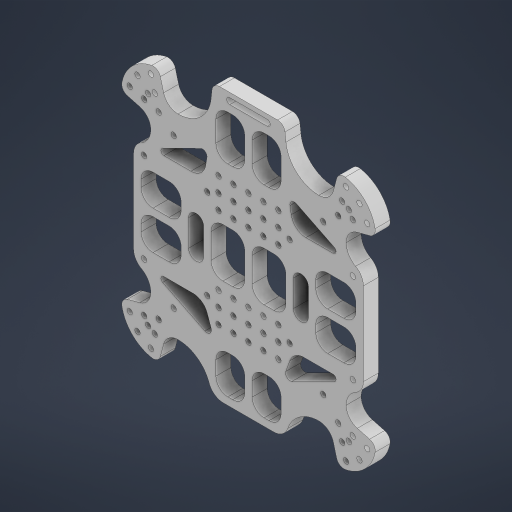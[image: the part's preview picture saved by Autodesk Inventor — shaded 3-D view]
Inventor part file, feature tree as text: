
AUTODESK INVENTOR PART (.ipt)
format: ipt  version: 2023 (Build 270158000, 158)  size: 738,816 bytes
history: native  units: mm
features: reference x147, extrude x5, fillet x4, sketch x4, other x4, plane x1
ambient origin geometry x8: Origin, YZ Plane, XZ Plane, XY Plane, X Axis, Y Axis, Z Axis, Center Point
bodies: Solid1 (feature_tree)
feature tree (165):
  plane  "Work Plane1"
  extrude  "Extrusion1"  Depth=10.0mm
  extrude  "Extrusion2"  Depth=10.0mm TaperAngle=0.0deg
  fillet  "Fillet1"  Radius=5.0mm
  extrude  "Extrusion3"  Depth=5.0mm
  extrude  "Extrusion4"  Depth=5.0mm
  extrude  "Extrusion5"  Depth=5.0mm
  fillet  "Fillet2"  Radius=5.0mm
  fillet  "Fillet3"  Radius=5.0mm
  fillet  "Fillet4"  Radius=5.0mm
  reference  "Reference1"
  reference  "Reference2"
  reference  "Reference3"
  reference  "Reference4"
  reference  "Reference5"
  reference  "Reference6"
  reference  "Reference7"
  reference  "Reference8"
  reference  "Reference9"
  reference  "Reference10"
  reference  "Reference11"
  reference  "Reference12"
  reference  "Reference13"
  reference  "Reference14"
  reference  "Reference15"
  reference  "Reference16"
  reference  "Reference17"
  reference  "Reference18"
  reference  "Reference19"
  reference  "Reference20"
  reference  "Reference21"
  reference  "Reference22"
  reference  "Reference23"
  reference  "Reference24"
  reference  "Reference25"
  reference  "Reference26"
  reference  "Reference27"
  reference  "Reference28"
  reference  "Reference29"
  reference  "Reference30"
  reference  "Reference31"
  reference  "Reference32"
  reference  "Reference33"
  reference  "Reference34"
  reference  "Reference35"
  reference  "Reference36"
  reference  "Reference37"
  reference  "Reference38"
  reference  "Reference39"
  reference  "Reference40"
  reference  "Reference41"
  reference  "Reference42"
  reference  "Reference43"
  reference  "Reference44"
  reference  "Reference45"
  reference  "Reference46"
  reference  "Reference47"
  reference  "Reference48"
  reference  "Reference49"
  reference  "Reference50"
  reference  "Reference51"
  reference  "Reference52"
  reference  "Reference53"
  reference  "Reference54"
  reference  "Reference55"
  reference  "Reference56"
  reference  "Reference57"
  reference  "Reference58"
  reference  "Reference59"
  reference  "Reference60"
  reference  "Reference61"
  reference  "Reference62"
  reference  "Reference63"
  reference  "Reference64"
  reference  "Reference65"
  reference  "Reference66"
  reference  "Reference67"
  reference  "Reference68"
  reference  "Reference69"
  reference  "Reference70"
  reference  "Reference71"
  reference  "Reference72"
  reference  "Reference73"
  reference  "Reference74"
  reference  "Reference75"
  reference  "Reference76"
  reference  "Reference77"
  reference  "Reference78"
  reference  "Reference79"
  reference  "Reference80"
  reference  "Reference81"
  reference  "Reference82"
  reference  "Reference83"
  reference  "Reference84"
  reference  "Reference85"
  reference  "Reference86"
  reference  "Reference87"
  reference  "Reference88"
  reference  "Reference89"
  reference  "Reference90"
  reference  "Reference91"
  reference  "Reference92"
  reference  "Reference93"
  reference  "Reference94"
  reference  "Reference95"
  reference  "Reference96"
  reference  "Reference97"
  reference  "Reference98"
  reference  "Reference99"
  reference  "Reference100"
  reference  "Reference101"
  reference  "Reference102"
  reference  "Reference103"
  reference  "Reference104"
  reference  "Reference105"
  reference  "Reference106"
  reference  "Reference107"
  reference  "Reference108"
  reference  "Reference109"
  reference  "Reference110"
  reference  "Reference111"
  reference  "Reference112"
  reference  "Reference113"
  reference  "Reference114"
  reference  "Reference115"
  reference  "Reference116"
  reference  "Reference117"
  reference  "Reference118"
  reference  "Reference119"
  reference  "Reference120"
  reference  "Reference121"
  reference  "Reference122"
  reference  "Reference123"
  reference  "Reference124"
  reference  "Reference125"
  reference  "Reference126"
  reference  "Reference127"
  reference  "Reference128"
  sketch  "Sketch2"  dims[d6=3.5mm d7=30.0mm d9=10.0mm d10=50.0mm d12=10.0mm]
  reference  "Reference129"
  reference  "Reference130"
  reference  "Reference131"
  reference  "Reference132"
  reference  "Reference133"
  reference  "Reference134"
  reference  "Reference135"
  reference  "Reference136"
  reference  "Reference137"
  reference  "Reference138"
  reference  "Reference139"
  reference  "Reference140"
  reference  "Reference141"
  reference  "Reference142"
  reference  "Reference143"
  reference  "Reference144"
  reference  "Reference145"
  reference  "Reference146"
  reference  "Reference147"
  sketch  "Sketch3"  dims[d15=30.0mm d17=10.0mm d18=50.0mm d20=10.0mm d23=10.0mm d24=0.0mm d25=5.0mm]
  sketch  "Sketch4"  dims[d27=5.0mm d28=5.0mm]
  sketch  "Sketch5"  dims[d29=5.0mm d30=5.0mm d31=5.0mm d33=5.0mm d34=5.0mm d35=5.0mm d36=5.0mm d37=10.0mm d38=5.0mm d40=5.0mm d41=5.0mm d42=2.0mm d43=10.0mm d44=0.0mm d45=8.0mm d46=100.0mm d47=100.0mm d48=3.5mm d49=10.0mm d50=0.0mm d51=6.5mm d52=6.5mm d58=50.0mm d60=10.0mm d61=30.0mm d63=10.0mm d66=50.0mm d68=10.0mm d69=30.0mm d71=10.0mm d74=3.0mm d75=0.0mm d76=70.0mm d77=5.0mm d78=5.0mm d79=5.0mm d80=35.0mm d81=60.0mm d82=5.0mm d83=3.0mm d84=0.0mm d85=3.0mm d86=10.0mm d87=2.0mm]
  parser-record x1  (decoder bookkeeping rows leaked as tree rows — omitted from the tree; the rows remain in map.json)
  other  "total.iam"
  other  "bottom:1"
  other  "middle spacer top:1"
note: 1 file-system path scrubbed to <path> (originals preserved in map.json)
